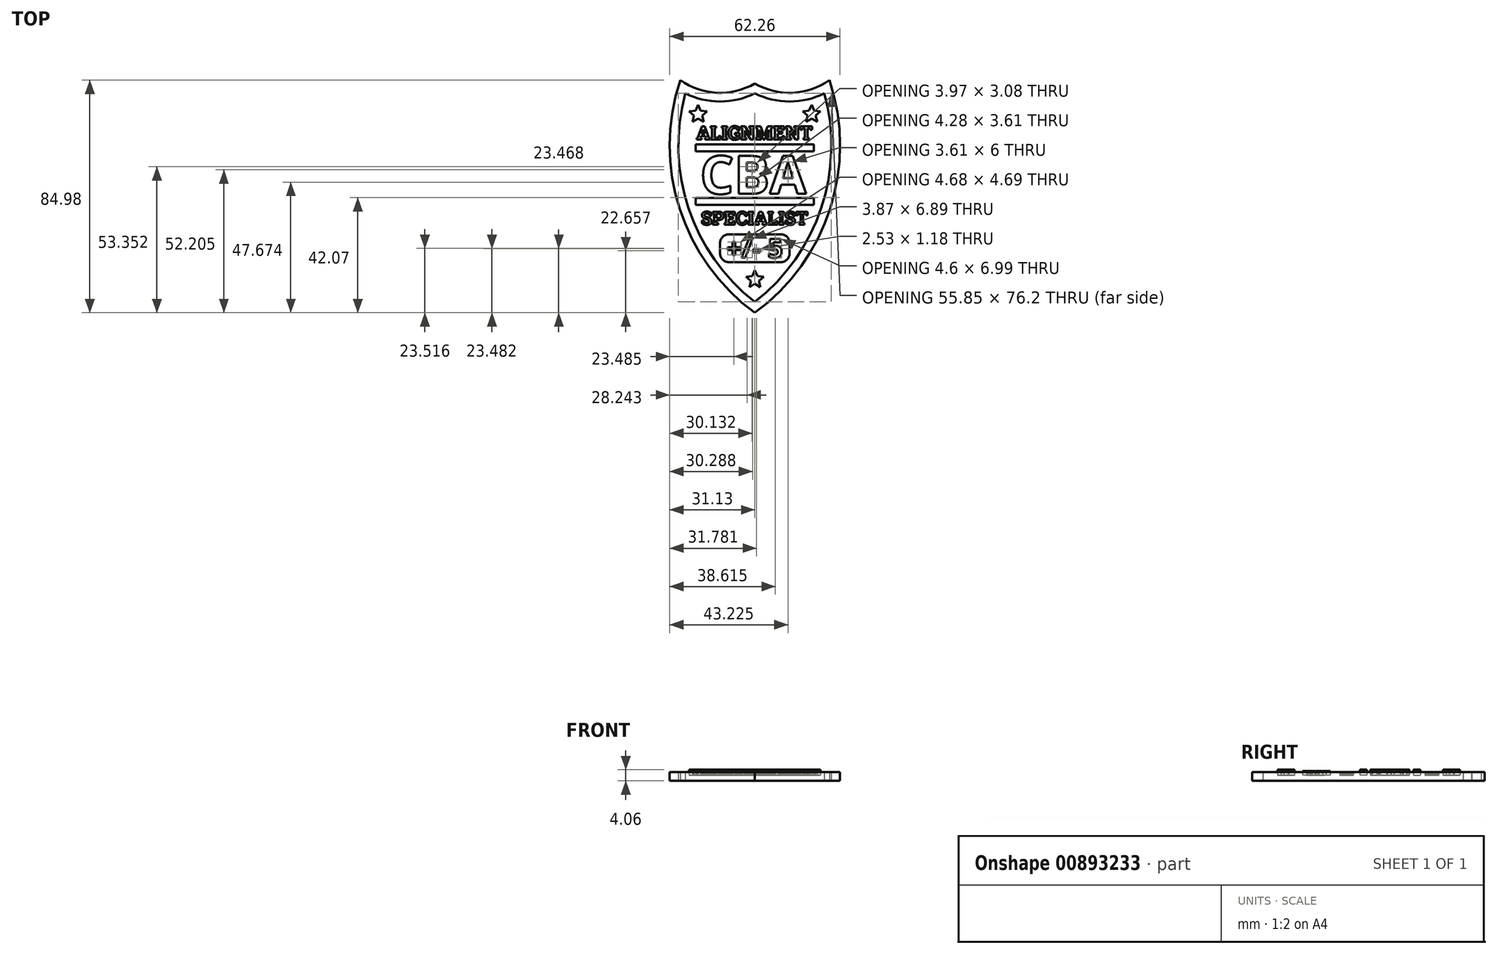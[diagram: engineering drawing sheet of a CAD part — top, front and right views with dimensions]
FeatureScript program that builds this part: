
annotation { "Feature Type Name" : "Feature", "Feature Type Description" : "" }
export const myFeature = defineFeature(function(context is Context, id is Id, definition is map)
    precondition{}
    {
        {
            var Q0;
            Q0=qCreatedBy(makeId("Top.planeOp"),FACE);
            cPlane(context, id + "F0", {"entities" : qUnion([Q0]), "cplaneType" : CPlaneType.OFFSET, "offset" : 2.03 * mm, "width" : 152.4 * mm, "height" : 152.4 * mm});
        }
        {
            var Q0;
            Q0=qCreatedBy(makeId("Top.planeOp"),FACE);
            var sketch = newSketch(context, id + "F1", { "sketchPlane" : qUnion([Q0])});
            skLineSegment(sketch, "E0.bottom", {"start": v(-25.4, 38.1) * mm, "end": v(25.4, 38.1) * mm, "construction": true});
            skLineSegment(sketch, "E0.top", {"start": v(-25.4, -38.1) * mm, "end": v(25.4, -38.1) * mm, "construction": true});
            skLineSegment(sketch, "E0.left", {"start": v(-25.4, 38.1) * mm, "end": v(-25.4, -38.1) * mm, "construction": true});
            skLineSegment(sketch, "E0.right", {"start": v(25.4, 38.1) * mm, "end": v(25.4, -38.1) * mm, "construction": true});
            skPoint(sketch, "E0.middle", {"position": v(0, 0) * mm});
            skLineSegment(sketch, "E1", {"start": v(0, 38.1) * mm, "end": v(0, 63.5) * mm, "construction": true});
            skPoint(sketch, "E1.endSnap0", {"position": v(0, 43.6) * mm});
            skLineSegment(sketch, "E2", {"start": v(0, 63.5) * mm, "end": v(12.7, 63.5) * mm, "construction": true});
            skLineSegment(sketch, "E3", {"start": v(12.7, 63.5) * mm, "end": v(0, 63.5) * mm, "construction": true});
            skArc(sketch, "E4", {"start": v(0, 38.1) * mm, "mid": v(12.7, 35.1) * mm, "end": v(25.4, 38.1) * mm});
            skArc(sketch, "E5", {"start": v(-25.4, 38.1) * mm, "mid": v(-15.62, 8.14) * mm, "end": v(9.94, -10.29) * mm, "construction": true});
            skArc(sketch, "E6", {"start": v(0, -38.1) * mm, "mid": v(24.24, -3.85) * mm, "end": v(25.4, 38.1) * mm});
            skLineSegment(sketch, "E7", {"start": v(0, 38.1) * mm, "end": v(0, -38.1) * mm});
            skArc(sketch, "E8.MirrorCS", {"start": v(0, -38.1) * mm, "mid": v(-24.24, -3.85) * mm, "end": v(-25.4, 38.1) * mm});
            skArc(sketch, "E9.MirrorCS", {"start": v(0, 38.1) * mm, "mid": v(-12.7, 35.1) * mm, "end": v(-25.4, 38.1) * mm});
            skSolve(sketch);
        }
        {
            var Q0;
            Q0=qCreatedBy(makeId("Top.planeOp"),FACE);
            var sketch = newSketch(context, id + "F2", { "sketchPlane" : qUnion([Q0])});
            skArc(sketch, "E10.0", {"start": v(0, 38.1) * mm, "mid": v(-12.7, 35.1) * mm, "end": v(-25.4, 38.1) * mm});
            skArc(sketch, "E11.0", {"start": v(0, 38.1) * mm, "mid": v(12.7, 35.1) * mm, "end": v(25.4, 38.1) * mm});
            skArc(sketch, "E12.0", {"start": v(0, -38.1) * mm, "mid": v(24.24, -3.85) * mm, "end": v(25.4, 38.1) * mm});
            skArc(sketch, "E13.0", {"start": v(0, -38.1) * mm, "mid": v(-24.24, -3.85) * mm, "end": v(-25.4, 38.1) * mm});
            skArc(sketch, "E14.0", {"start": v(0, 41.7) * mm, "mid": v(-13.8, 38.3) * mm, "end": v(-27.26, 42.9) * mm});
            skArc(sketch, "E14.1", {"start": v(0, 41.7) * mm, "mid": v(13.8, 38.3) * mm, "end": v(27.26, 42.9) * mm});
            skArc(sketch, "E14.2", {"start": v(0, -42.07) * mm, "mid": v(27.51, -4.04) * mm, "end": v(27.26, 42.9) * mm});
            skArc(sketch, "E14.3", {"start": v(0, -42.07) * mm, "mid": v(-27.51, -4.04) * mm, "end": v(-27.26, 42.9) * mm});
            skSolve(sketch);
        }
        {
            var Q0;
            Q0 = qSketchRegion(id + "F2", true);
            extrude(context, id + "F3", {"entities" : qUnion([Q0]), "depth" : 3.17 * mm, "offsetDistance" : 25.4 * mm});
        }
        {
            var Q0;
            Q0=qCreatedBy(id+"F0.planeOp",FACE);
            var sketch = newSketch(context, id + "F4", { "sketchPlane" : qUnion([Q0])});
            skLineSegment(sketch, "E15", {"start": v(-25.4, 15.35) * mm, "end": v(22.36, 15.35) * mm, "construction": true});
            skLineSegment(sketch, "E16", {"start": v(22.36, 15.35) * mm, "end": v(22.36, 1.37) * mm, "construction": true});
            skLineSegment(sketch, "E17", {"start": v(22.36, 1.37) * mm, "end": v(-25.4, 1.37) * mm, "construction": true});
            skLineSegment(sketch, "E18", {"start": v(-25.4, 1.37) * mm, "end": v(-25.4, 15.35) * mm, "construction": true});
            skText(sketch, "E19", { "text": "CBA", "fontName": "OpenSans-Bold.ttf"});
            skLineSegment(sketch, "E20", {"start": v(0, 0) * mm, "end": v(0, 38.1) * mm, "construction": true});
            skLineSegment(sketch, "E21.0", {"start": v(-21.59, 16.88) * mm, "end": v(21.6, 16.88) * mm});
            skLineSegment(sketch, "E22", {"start": v(-21.59, 16.88) * mm, "end": v(-21.59, 19.42) * mm});
            skLineSegment(sketch, "E23", {"start": v(-21.59, 19.42) * mm, "end": v(0, 19.42) * mm});
            skLineSegment(sketch, "E24", {"start": v(0, 19.42) * mm, "end": v(21.59, 19.42) * mm});
            skLineSegment(sketch, "E25", {"start": v(21.59, 19.42) * mm, "end": v(21.59, 16.88) * mm});
            skLineSegment(sketch, "E26", {"start": v(0, 15.35) * mm, "end": v(0, 1.37) * mm, "construction": true});
            skLineSegment(sketch, "E27", {"start": v(0, 8.36) * mm, "end": v(22.36, 8.36) * mm, "construction": true});
            skLineSegment(sketch, "E28.MirrorCS", {"start": v(-21.6, -2.69) * mm, "end": v(0, -2.69) * mm});
            skLineSegment(sketch, "E29.MirrorCS", {"start": v(0, -2.69) * mm, "end": v(21.59, -2.69) * mm});
            skLineSegment(sketch, "E30.MirrorCS", {"start": v(21.59, -2.69) * mm, "end": v(21.59, -0.15) * mm});
            skLineSegment(sketch, "E31.MirrorCS", {"start": v(-21.6, -0.15) * mm, "end": v(-21.6, -2.69) * mm});
            skLineSegment(sketch, "E32.MirrorCS", {"start": v(-21.59, -0.15) * mm, "end": v(21.59, -0.15) * mm});
            skCircle(sketch, "E33.cCircle", {"center": v(0, -29.93) * mm, "radius": 3.42 * mm, "construction": true});
            skLineSegment(sketch, "E33.0", {"start": v(0, -26.51) * mm, "end": v(3.25, -28.88) * mm, "construction": true});
            skLineSegment(sketch, "E33.1", {"start": v(3.25, -28.88) * mm, "end": v(2.01, -32.7) * mm, "construction": true});
            skLineSegment(sketch, "E33.2", {"start": v(2.01, -32.7) * mm, "end": v(-2.01, -32.7) * mm, "construction": true});
            skLineSegment(sketch, "E33.3", {"start": v(-2.01, -32.7) * mm, "end": v(-3.25, -28.88) * mm, "construction": true});
            skLineSegment(sketch, "E33.4", {"start": v(-3.25, -28.88) * mm, "end": v(0, -26.51) * mm, "construction": true});
            skCircle(sketch, "E34.cCircle", {"center": v(0, -29.93) * mm, "radius": 1.35 * mm, "construction": true});
            skLineSegment(sketch, "E34.0", {"start": v(0, -28.58) * mm, "end": v(1.28, -29.52) * mm, "construction": true});
            skLineSegment(sketch, "E34.1", {"start": v(1.28, -29.52) * mm, "end": v(0.8, -31.03) * mm, "construction": true});
            skLineSegment(sketch, "E34.2", {"start": v(0.8, -31.03) * mm, "end": v(-0.8, -31.03) * mm, "construction": true});
            skLineSegment(sketch, "E34.3", {"start": v(-0.8, -31.03) * mm, "end": v(-1.28, -29.52) * mm, "construction": true});
            skLineSegment(sketch, "E34.4", {"start": v(-1.28, -29.52) * mm, "end": v(0, -28.58) * mm, "construction": true});
            skLineSegment(sketch, "E35", {"start": v(-1.28, -29.52) * mm, "end": v(0, -26.51) * mm, "construction": true});
            skLineSegment(sketch, "E36", {"start": v(1.28, -29.52) * mm, "end": v(0, -26.51) * mm, "construction": true});
            skLineSegment(sketch, "E37", {"start": v(0, -28.58) * mm, "end": v(3.25, -28.88) * mm, "construction": true});
            skLineSegment(sketch, "E38", {"start": v(3.25, -28.88) * mm, "end": v(0.9, -30.95) * mm, "construction": true});
            skLineSegment(sketch, "E39", {"start": v(0.9, -30.95) * mm, "end": v(1.28, -29.52) * mm, "construction": true});
            skLineSegment(sketch, "E40", {"start": v(2.01, -32.7) * mm, "end": v(1.28, -29.52) * mm, "construction": true});
            skLineSegment(sketch, "E41", {"start": v(-0.8, -31.03) * mm, "end": v(2.01, -32.7) * mm, "construction": true});
            skLineSegment(sketch, "E42", {"start": v(-2.01, -32.7) * mm, "end": v(-1.28, -29.52) * mm, "construction": true});
            skLineSegment(sketch, "E43", {"start": v(-2.01, -32.7) * mm, "end": v(0.8, -31.03) * mm, "construction": true});
            skLineSegment(sketch, "E44", {"start": v(0, -28.58) * mm, "end": v(-3.25, -28.88) * mm, "construction": true});
            skLineSegment(sketch, "E45", {"start": v(-0.8, -31.03) * mm, "end": v(-3.25, -28.88) * mm, "construction": true});
            skLineSegment(sketch, "E46", {"start": v(-3.25, -28.88) * mm, "end": v(-0.92, -28.66) * mm});
            skLineSegment(sketch, "E47", {"start": v(-0.92, -28.66) * mm, "end": v(0, -26.51) * mm});
            skLineSegment(sketch, "E48", {"start": v(0, -26.51) * mm, "end": v(0.93, -28.67) * mm});
            skLineSegment(sketch, "E49", {"start": v(0.93, -28.67) * mm, "end": v(3.25, -28.88) * mm});
            skLineSegment(sketch, "E50", {"start": v(3.25, -28.88) * mm, "end": v(1.5, -30.42) * mm});
            skLineSegment(sketch, "E51", {"start": v(1.5, -30.42) * mm, "end": v(2.01, -32.7) * mm});
            skLineSegment(sketch, "E52", {"start": v(2.01, -32.7) * mm, "end": v(0, -31.5) * mm});
            skLineSegment(sketch, "E53", {"start": v(0, -31.5) * mm, "end": v(-2.01, -32.7) * mm});
            skLineSegment(sketch, "E54", {"start": v(-2.01, -32.7) * mm, "end": v(-1.5, -30.42) * mm});
            skLineSegment(sketch, "E55", {"start": v(-1.5, -30.42) * mm, "end": v(-3.25, -28.88) * mm});
            skArc(sketch, "E56.0", {"start": v(3.9, -33.09) * mm, "mid": v(-18.21, -1.84) * mm, "end": v(-19.27, 36.43) * mm, "construction": true});
            skLineSegment(sketch, "E57", {"start": v(0, 0) * mm, "end": v(-21.6, 0) * mm, "construction": true});
            skLineSegment(sketch, "E58", {"start": v(-21.6, 0) * mm, "end": v(-21.6, 5.6) * mm, "construction": true});
            skLineSegment(sketch, "E59", {"start": v(-21.6, 5.6) * mm, "end": v(-20.22, 5.6) * mm, "construction": true});
            skCircle(sketch, "E60.cCircle", {"center": v(-20.36, 5.58) * mm, "radius": 3.42 * mm, "construction": true});
            skLineSegment(sketch, "E60.0", {"start": v(-20.36, 9) * mm, "end": v(-17.11, 6.64) * mm, "construction": true});
            skLineSegment(sketch, "E60.1", {"start": v(-17.11, 6.64) * mm, "end": v(-18.35, 2.81) * mm, "construction": true});
            skLineSegment(sketch, "E60.2", {"start": v(-18.35, 2.81) * mm, "end": v(-22.37, 2.81) * mm, "construction": true});
            skLineSegment(sketch, "E60.3", {"start": v(-22.37, 2.81) * mm, "end": v(-23.62, 6.64) * mm, "construction": true});
            skLineSegment(sketch, "E60.4", {"start": v(-23.62, 6.64) * mm, "end": v(-20.36, 9) * mm, "construction": true});
            skCircle(sketch, "E61.cCircle", {"center": v(-20.36, 5.58) * mm, "radius": 1.35 * mm, "construction": true});
            skLineSegment(sketch, "E61.0", {"start": v(-20.36, 6.93) * mm, "end": v(-19.08, 6) * mm, "construction": true});
            skLineSegment(sketch, "E61.1", {"start": v(-19.08, 6) * mm, "end": v(-19.57, 4.49) * mm, "construction": true});
            skLineSegment(sketch, "E61.2", {"start": v(-19.57, 4.49) * mm, "end": v(-21.16, 4.49) * mm, "construction": true});
            skLineSegment(sketch, "E61.3", {"start": v(-21.16, 4.49) * mm, "end": v(-21.65, 6) * mm, "construction": true});
            skLineSegment(sketch, "E61.4", {"start": v(-21.65, 6) * mm, "end": v(-20.36, 6.93) * mm, "construction": true});
            skLineSegment(sketch, "E62", {"start": v(-21.65, 6) * mm, "end": v(-20.36, 9) * mm, "construction": true});
            skLineSegment(sketch, "E63", {"start": v(-19.08, 6) * mm, "end": v(-20.36, 9) * mm, "construction": true});
            skLineSegment(sketch, "E64", {"start": v(-20.36, 6.93) * mm, "end": v(-17.11, 6.64) * mm, "construction": true});
            skLineSegment(sketch, "E65", {"start": v(-17.11, 6.64) * mm, "end": v(-19.47, 4.57) * mm, "construction": true});
            skLineSegment(sketch, "E66", {"start": v(-19.47, 4.57) * mm, "end": v(-19.08, 6) * mm, "construction": true});
            skLineSegment(sketch, "E67", {"start": v(-18.35, 2.81) * mm, "end": v(-19.08, 6) * mm, "construction": true});
            skLineSegment(sketch, "E68", {"start": v(-21.16, 4.49) * mm, "end": v(-18.35, 2.81) * mm, "construction": true});
            skLineSegment(sketch, "E69", {"start": v(-22.37, 2.81) * mm, "end": v(-21.65, 6) * mm, "construction": true});
            skLineSegment(sketch, "E70", {"start": v(-22.37, 2.81) * mm, "end": v(-19.57, 4.49) * mm, "construction": true});
            skLineSegment(sketch, "E71", {"start": v(-20.36, 6.93) * mm, "end": v(-23.62, 6.64) * mm, "construction": true});
            skLineSegment(sketch, "E72", {"start": v(-21.16, 4.49) * mm, "end": v(-23.62, 6.64) * mm, "construction": true});
            skLineSegment(sketch, "E73", {"start": v(-23.62, 6.64) * mm, "end": v(-21.28, 6.85) * mm, "construction": true});
            skLineSegment(sketch, "E74", {"start": v(-21.28, 6.85) * mm, "end": v(-20.36, 9) * mm, "construction": true});
            skLineSegment(sketch, "E75", {"start": v(-20.36, 9) * mm, "end": v(-19.44, 6.85) * mm, "construction": true});
            skLineSegment(sketch, "E76", {"start": v(-19.44, 6.85) * mm, "end": v(-17.11, 6.64) * mm, "construction": true});
            skLineSegment(sketch, "E77", {"start": v(-17.11, 6.64) * mm, "end": v(-18.87, 5.1) * mm, "construction": true});
            skLineSegment(sketch, "E78", {"start": v(-18.87, 5.1) * mm, "end": v(-18.35, 2.81) * mm, "construction": true});
            skLineSegment(sketch, "E79", {"start": v(-18.35, 2.81) * mm, "end": v(-20.36, 4.02) * mm, "construction": true});
            skLineSegment(sketch, "E80", {"start": v(-20.36, 4.02) * mm, "end": v(-22.37, 2.81) * mm, "construction": true});
            skLineSegment(sketch, "E81", {"start": v(-22.37, 2.81) * mm, "end": v(-21.85, 5.1) * mm, "construction": true});
            skLineSegment(sketch, "E82", {"start": v(-21.85, 5.1) * mm, "end": v(-23.62, 6.64) * mm, "construction": true});
            skCircle(sketch, "E83.MirrorC", {"center": v(20.36, 5.58) * mm, "radius": 1.35 * mm, "construction": true});
            skLineSegment(sketch, "E84.MirrorCS", {"start": v(22.37, 2.81) * mm, "end": v(21.85, 5.1) * mm, "construction": true});
            skLineSegment(sketch, "E85.MirrorCS", {"start": v(21.85, 5.1) * mm, "end": v(23.62, 6.64) * mm, "construction": true});
            skLineSegment(sketch, "E86.MirrorCS", {"start": v(17.11, 6.64) * mm, "end": v(18.87, 5.1) * mm, "construction": true});
            skLineSegment(sketch, "E87.MirrorCS", {"start": v(19.44, 6.85) * mm, "end": v(17.11, 6.64) * mm, "construction": true});
            skLineSegment(sketch, "E88.MirrorCS", {"start": v(23.62, 6.64) * mm, "end": v(21.28, 6.85) * mm, "construction": true});
            skLineSegment(sketch, "E89.MirrorCS", {"start": v(20.36, 9) * mm, "end": v(19.44, 6.85) * mm, "construction": true});
            skLineSegment(sketch, "E90.MirrorCS", {"start": v(20.36, 4.02) * mm, "end": v(22.37, 2.81) * mm, "construction": true});
            skLineSegment(sketch, "E91.MirrorCS", {"start": v(18.87, 5.1) * mm, "end": v(18.35, 2.81) * mm, "construction": true});
            skLineSegment(sketch, "E92.MirrorCS", {"start": v(18.35, 2.81) * mm, "end": v(20.36, 4.02) * mm, "construction": true});
            skLineSegment(sketch, "E93.MirrorCS", {"start": v(21.28, 6.85) * mm, "end": v(20.36, 9) * mm, "construction": true});
            skLineSegment(sketch, "E94.MirrorCS", {"start": v(19.08, 6) * mm, "end": v(20.36, 9) * mm, "construction": true});
            skLineSegment(sketch, "E95.MirrorCS", {"start": v(17.11, 6.64) * mm, "end": v(19.47, 4.57) * mm, "construction": true});
            skLineSegment(sketch, "E96.MirrorCS", {"start": v(21.16, 4.49) * mm, "end": v(23.62, 6.64) * mm, "construction": true});
            skLineSegment(sketch, "E97.MirrorCS", {"start": v(20.36, 6.93) * mm, "end": v(19.08, 6) * mm, "construction": true});
            skLineSegment(sketch, "E98.MirrorCS", {"start": v(20.36, 6.93) * mm, "end": v(23.62, 6.64) * mm, "construction": true});
            skLineSegment(sketch, "E99.MirrorCS", {"start": v(18.35, 2.81) * mm, "end": v(22.37, 2.81) * mm, "construction": true});
            skCircle(sketch, "E100.MirrorC", {"center": v(20.36, 5.58) * mm, "radius": 3.42 * mm, "construction": true});
            skLineSegment(sketch, "E101.MirrorCS", {"start": v(22.37, 2.81) * mm, "end": v(19.57, 4.49) * mm, "construction": true});
            skLineSegment(sketch, "E102.MirrorCS", {"start": v(21.16, 4.49) * mm, "end": v(18.35, 2.81) * mm, "construction": true});
            skLineSegment(sketch, "E103.MirrorCS", {"start": v(21.65, 6) * mm, "end": v(20.36, 9) * mm, "construction": true});
            skLineSegment(sketch, "E104.MirrorCS", {"start": v(20.36, 9) * mm, "end": v(17.11, 6.64) * mm, "construction": true});
            skLineSegment(sketch, "E105.MirrorCS", {"start": v(20.36, 6.93) * mm, "end": v(17.11, 6.64) * mm, "construction": true});
            skLineSegment(sketch, "E106.MirrorCS", {"start": v(22.37, 2.81) * mm, "end": v(23.62, 6.64) * mm, "construction": true});
            skLineSegment(sketch, "E107.MirrorCS", {"start": v(23.62, 6.64) * mm, "end": v(20.36, 9) * mm, "construction": true});
            skLineSegment(sketch, "E108.MirrorCS", {"start": v(21.6, 5.6) * mm, "end": v(20.22, 5.6) * mm, "construction": true});
            skLineSegment(sketch, "E109.MirrorCS", {"start": v(19.57, 4.49) * mm, "end": v(21.16, 4.49) * mm, "construction": true});
            skLineSegment(sketch, "E110.MirrorCS", {"start": v(21.16, 4.49) * mm, "end": v(21.65, 6) * mm, "construction": true});
            skLineSegment(sketch, "E111.MirrorCS", {"start": v(19.08, 6) * mm, "end": v(19.57, 4.49) * mm, "construction": true});
            skLineSegment(sketch, "E112.MirrorCS", {"start": v(18.35, 2.81) * mm, "end": v(19.08, 6) * mm, "construction": true});
            skLineSegment(sketch, "E113.MirrorCS", {"start": v(19.47, 4.57) * mm, "end": v(19.08, 6) * mm, "construction": true});
            skLineSegment(sketch, "E114.MirrorCS", {"start": v(17.11, 6.64) * mm, "end": v(18.35, 2.81) * mm, "construction": true});
            skLineSegment(sketch, "E115.MirrorCS", {"start": v(22.37, 2.81) * mm, "end": v(21.65, 6) * mm, "construction": true});
            skLineSegment(sketch, "E116.MirrorCS", {"start": v(21.65, 6) * mm, "end": v(20.36, 6.93) * mm, "construction": true});
            skLineSegment(sketch, "E117", {"start": v(-20.6, 30.48) * mm, "end": v(0, 30.48) * mm, "construction": true});
            skLineSegment(sketch, "E118", {"start": v(-21.98, 30.48) * mm, "end": v(-20.6, 30.48) * mm, "construction": true});
            skCircle(sketch, "E119.cCircle", {"center": v(-20.75, 30.46) * mm, "radius": 3.42 * mm, "construction": true});
            skLineSegment(sketch, "E119.0", {"start": v(-20.75, 33.89) * mm, "end": v(-17.5, 31.52) * mm, "construction": true});
            skLineSegment(sketch, "E119.1", {"start": v(-17.5, 31.52) * mm, "end": v(-18.74, 27.7) * mm, "construction": true});
            skLineSegment(sketch, "E119.2", {"start": v(-18.74, 27.7) * mm, "end": v(-22.76, 27.7) * mm, "construction": true});
            skLineSegment(sketch, "E119.3", {"start": v(-22.76, 27.7) * mm, "end": v(-24, 31.52) * mm, "construction": true});
            skLineSegment(sketch, "E119.4", {"start": v(-24, 31.52) * mm, "end": v(-20.75, 33.89) * mm, "construction": true});
            skCircle(sketch, "E120.cCircle", {"center": v(-20.75, 30.46) * mm, "radius": 1.35 * mm, "construction": true});
            skLineSegment(sketch, "E120.0", {"start": v(-20.75, 31.82) * mm, "end": v(-19.47, 30.88) * mm, "construction": true});
            skLineSegment(sketch, "E120.1", {"start": v(-19.47, 30.88) * mm, "end": v(-19.96, 29.37) * mm, "construction": true});
            skLineSegment(sketch, "E120.2", {"start": v(-19.96, 29.37) * mm, "end": v(-21.55, 29.37) * mm, "construction": true});
            skLineSegment(sketch, "E120.3", {"start": v(-21.55, 29.37) * mm, "end": v(-22.04, 30.88) * mm, "construction": true});
            skLineSegment(sketch, "E120.4", {"start": v(-22.04, 30.88) * mm, "end": v(-20.75, 31.82) * mm, "construction": true});
            skLineSegment(sketch, "E121", {"start": v(-22.04, 30.88) * mm, "end": v(-20.75, 33.89) * mm, "construction": true});
            skLineSegment(sketch, "E122", {"start": v(-19.47, 30.88) * mm, "end": v(-20.75, 33.89) * mm, "construction": true});
            skLineSegment(sketch, "E123", {"start": v(-20.75, 31.82) * mm, "end": v(-17.5, 31.52) * mm, "construction": true});
            skLineSegment(sketch, "E124", {"start": v(-17.5, 31.52) * mm, "end": v(-19.86, 29.45) * mm, "construction": true});
            skLineSegment(sketch, "E125", {"start": v(-19.86, 29.45) * mm, "end": v(-19.47, 30.88) * mm, "construction": true});
            skLineSegment(sketch, "E126", {"start": v(-18.74, 27.7) * mm, "end": v(-19.47, 30.88) * mm, "construction": true});
            skLineSegment(sketch, "E127", {"start": v(-21.55, 29.37) * mm, "end": v(-18.74, 27.7) * mm, "construction": true});
            skLineSegment(sketch, "E128", {"start": v(-22.76, 27.7) * mm, "end": v(-22.04, 30.88) * mm, "construction": true});
            skLineSegment(sketch, "E129", {"start": v(-22.76, 27.7) * mm, "end": v(-19.96, 29.37) * mm, "construction": true});
            skLineSegment(sketch, "E130", {"start": v(-20.75, 31.82) * mm, "end": v(-24, 31.52) * mm, "construction": true});
            skLineSegment(sketch, "E131", {"start": v(-21.55, 29.37) * mm, "end": v(-24, 31.52) * mm, "construction": true});
            skLineSegment(sketch, "E132", {"start": v(-24, 31.52) * mm, "end": v(-21.67, 31.73) * mm});
            skLineSegment(sketch, "E133", {"start": v(-21.67, 31.73) * mm, "end": v(-20.75, 33.89) * mm});
            skLineSegment(sketch, "E134", {"start": v(-20.75, 33.89) * mm, "end": v(-19.83, 31.73) * mm});
            skLineSegment(sketch, "E135", {"start": v(-19.83, 31.73) * mm, "end": v(-17.5, 31.52) * mm});
            skLineSegment(sketch, "E136", {"start": v(-17.5, 31.52) * mm, "end": v(-19.26, 29.98) * mm});
            skLineSegment(sketch, "E137", {"start": v(-19.26, 29.98) * mm, "end": v(-18.74, 27.7) * mm});
            skLineSegment(sketch, "E138", {"start": v(-18.74, 27.7) * mm, "end": v(-20.75, 28.9) * mm});
            skLineSegment(sketch, "E139", {"start": v(-20.75, 28.9) * mm, "end": v(-22.76, 27.7) * mm});
            skLineSegment(sketch, "E140", {"start": v(-22.76, 27.7) * mm, "end": v(-22.24, 29.98) * mm});
            skLineSegment(sketch, "E141", {"start": v(-22.24, 29.98) * mm, "end": v(-24, 31.52) * mm});
            skLineSegment(sketch, "E142.MirrorCS", {"start": v(17.5, 31.52) * mm, "end": v(19.26, 29.98) * mm});
            skLineSegment(sketch, "E143.MirrorCS", {"start": v(19.86, 29.45) * mm, "end": v(19.47, 30.88) * mm, "construction": true});
            skLineSegment(sketch, "E144.MirrorCS", {"start": v(20.75, 31.82) * mm, "end": v(19.47, 30.88) * mm, "construction": true});
            skLineSegment(sketch, "E145.MirrorCS", {"start": v(21.98, 30.48) * mm, "end": v(20.6, 30.48) * mm, "construction": true});
            skLineSegment(sketch, "E146.MirrorCS", {"start": v(22.04, 30.88) * mm, "end": v(20.75, 31.82) * mm, "construction": true});
            skLineSegment(sketch, "E147.MirrorCS", {"start": v(19.47, 30.88) * mm, "end": v(19.96, 29.37) * mm, "construction": true});
            skLineSegment(sketch, "E148.MirrorCS", {"start": v(21.55, 29.37) * mm, "end": v(22.04, 30.88) * mm, "construction": true});
            skLineSegment(sketch, "E149.MirrorCS", {"start": v(19.96, 29.37) * mm, "end": v(21.55, 29.37) * mm, "construction": true});
            skCircle(sketch, "E150.MirrorC", {"center": v(20.75, 30.46) * mm, "radius": 1.35 * mm, "construction": true});
            skLineSegment(sketch, "E151.MirrorCS", {"start": v(17.5, 31.52) * mm, "end": v(19.86, 29.45) * mm, "construction": true});
            skLineSegment(sketch, "E152.MirrorCS", {"start": v(19.26, 29.98) * mm, "end": v(18.74, 27.7) * mm});
            skLineSegment(sketch, "E153.MirrorCS", {"start": v(22.24, 29.98) * mm, "end": v(24, 31.52) * mm});
            skLineSegment(sketch, "E154.MirrorCS", {"start": v(18.74, 27.7) * mm, "end": v(20.75, 28.9) * mm});
            skLineSegment(sketch, "E155.MirrorCS", {"start": v(21.55, 29.37) * mm, "end": v(18.74, 27.7) * mm, "construction": true});
            skLineSegment(sketch, "E156.MirrorCS", {"start": v(21.55, 29.37) * mm, "end": v(24, 31.52) * mm, "construction": true});
            skLineSegment(sketch, "E157.MirrorCS", {"start": v(18.74, 27.7) * mm, "end": v(19.47, 30.88) * mm, "construction": true});
            skLineSegment(sketch, "E158.MirrorCS", {"start": v(24, 31.52) * mm, "end": v(21.67, 31.73) * mm});
            skLineSegment(sketch, "E159.MirrorCS", {"start": v(20.75, 33.89) * mm, "end": v(19.83, 31.73) * mm});
            skLineSegment(sketch, "E160.MirrorCS", {"start": v(22.76, 27.7) * mm, "end": v(22.24, 29.98) * mm});
            skLineSegment(sketch, "E161.MirrorCS", {"start": v(21.67, 31.73) * mm, "end": v(20.75, 33.89) * mm});
            skLineSegment(sketch, "E162.MirrorCS", {"start": v(20.75, 28.9) * mm, "end": v(22.76, 27.7) * mm});
            skLineSegment(sketch, "E163.MirrorCS", {"start": v(19.83, 31.73) * mm, "end": v(17.5, 31.52) * mm});
            skLineSegment(sketch, "E164.MirrorCS", {"start": v(22.04, 30.88) * mm, "end": v(20.75, 33.89) * mm, "construction": true});
            skLineSegment(sketch, "E165.MirrorCS", {"start": v(22.76, 27.7) * mm, "end": v(19.96, 29.37) * mm, "construction": true});
            skLineSegment(sketch, "E166.MirrorCS", {"start": v(18.74, 27.7) * mm, "end": v(22.76, 27.7) * mm, "construction": true});
            skLineSegment(sketch, "E167.MirrorCS", {"start": v(20.75, 31.82) * mm, "end": v(17.5, 31.52) * mm, "construction": true});
            skLineSegment(sketch, "E168.MirrorCS", {"start": v(20.75, 31.82) * mm, "end": v(24, 31.52) * mm, "construction": true});
            skLineSegment(sketch, "E169.MirrorCS", {"start": v(22.76, 27.7) * mm, "end": v(24, 31.52) * mm, "construction": true});
            skLineSegment(sketch, "E170.MirrorCS", {"start": v(22.76, 27.7) * mm, "end": v(22.04, 30.88) * mm, "construction": true});
            skLineSegment(sketch, "E171.MirrorCS", {"start": v(17.5, 31.52) * mm, "end": v(18.74, 27.7) * mm, "construction": true});
            skLineSegment(sketch, "E172.MirrorCS", {"start": v(19.47, 30.88) * mm, "end": v(20.75, 33.89) * mm, "construction": true});
            skLineSegment(sketch, "E173.MirrorCS", {"start": v(20.75, 33.89) * mm, "end": v(17.5, 31.52) * mm, "construction": true});
            skLineSegment(sketch, "E174.MirrorCS", {"start": v(24, 31.52) * mm, "end": v(20.75, 33.89) * mm, "construction": true});
            skCircle(sketch, "E175.MirrorC", {"center": v(20.75, 30.46) * mm, "radius": 3.42 * mm, "construction": true});
            const initialGuessF4  = {"E19": [-0.02004, 0.00137, 1, 0, 0.01398]};
            skSetInitialGuess(sketch, initialGuessF4);
            skSolve(sketch);
        }
        {
            var Q0;
            Q0 = qSketchRegion(id + "F4", true);
            extrude(context, id + "F5", {"entities" : qUnion([Q0]), "depth" : 2.03 * mm, "offsetDistance" : 25.4 * mm});
        }
        {
            var Q0;
            Q0=qCreatedBy(id+"F0.planeOp",FACE);
            var Q1;
            Q1=qCreatedBy(id+"F0.planeOp",FACE);
            var sketch = newSketch(context, id + "F6", { "sketchPlane" : qUnion([Q0, Q1])});
            skPoint(sketch, "E176.0", {"position": v(0, 0) * mm});
            skArc(sketch, "E177.0", {"start": v(0, -38.1) * mm, "mid": v(-24.24, -3.85) * mm, "end": v(-25.4, 38.1) * mm, "construction": true});
            skArc(sketch, "E178.0", {"start": v(0, -38.1) * mm, "mid": v(24.24, -3.85) * mm, "end": v(25.4, 38.1) * mm, "construction": true});
            skLineSegment(sketch, "E179", {"start": v(-25.4, 0) * mm, "end": v(25.4, 0) * mm, "construction": true});
            skLineSegment(sketch, "E180.bottom", {"start": v(9.53, -13.4) * mm, "end": v(-9.53, -13.4) * mm});
            skLineSegment(sketch, "E180.top", {"start": v(9.53, -23.56) * mm, "end": v(-9.53, -23.56) * mm});
            skLineSegment(sketch, "E180.left", {"start": v(12.7, -16.57) * mm, "end": v(12.7, -20.38) * mm});
            skLineSegment(sketch, "E180.right", {"start": v(-12.7, -16.57) * mm, "end": v(-12.7, -20.38) * mm});
            skPoint(sketch, "E180.middle", {"position": v(0, -18.48) * mm});
            skPoint(sketch, "E181.visualSharp", {"position": v(-12.7, -13.4) * mm});
            skArc(sketch, "E181.filletArc", {"start": v(-9.53, -13.4) * mm, "mid": v(-11.77, -14.33) * mm, "end": v(-12.7, -16.57) * mm});
            skPoint(sketch, "E182.visualSharp", {"position": v(-12.7, -23.56) * mm});
            skArc(sketch, "E182.filletArc", {"start": v(-12.7, -20.38) * mm, "mid": v(-11.77, -22.63) * mm, "end": v(-9.53, -23.56) * mm});
            skPoint(sketch, "E183.visualSharp", {"position": v(12.7, -13.4) * mm});
            skArc(sketch, "E183.filletArc", {"start": v(12.7, -16.57) * mm, "mid": v(11.77, -14.33) * mm, "end": v(9.53, -13.4) * mm});
            skPoint(sketch, "E184.visualSharp", {"position": v(12.7, -23.56) * mm});
            skArc(sketch, "E184.filletArc", {"start": v(9.53, -23.56) * mm, "mid": v(11.77, -22.63) * mm, "end": v(12.7, -20.38) * mm});
            skArc(sketch, "E185.0", {"start": v(20.74, 29.7) * mm, "mid": v(10.26, 28.84) * mm, "end": v(0, 31.16) * mm, "construction": true});
            skArc(sketch, "E185.1", {"start": v(0, -29.8) * mm, "mid": v(17.92, -2.69) * mm, "end": v(20.74, 29.7) * mm, "construction": true});
            skArc(sketch, "E185.2", {"start": v(-20.74, 29.7) * mm, "mid": v(-17.92, -2.69) * mm, "end": v(0, -29.8) * mm, "construction": true});
            skArc(sketch, "E185.3", {"start": v(0, 31.16) * mm, "mid": v(-10.26, 28.84) * mm, "end": v(-20.74, 29.7) * mm, "construction": true});
            skLineSegment(sketch, "E186", {"start": v(0, -15.06) * mm, "end": v(0, -13.4) * mm, "construction": true});
            skText(sketch, "E187", { "text": "+/- 5", "fontName": "OpenSans-Bold.ttf"});
            const initialGuessF6  = {"E187": [-0.0104, -0.022, 1, 0, 0.00695]};
            skSetInitialGuess(sketch, initialGuessF6);
            skSolve(sketch);
        }
        {
            var Q0;
            Q0 = qSketchRegion(id + "F6", true);
            extrude(context, id + "F7", {"entities" : qUnion([Q0]), "depth" : 1.52 * mm, "offsetDistance" : 25.4 * mm});
        }
        {
            var Q0;
            Q0=qCreatedBy(id+"F0.planeOp",FACE);
            var Q1;
            Q1=qCreatedBy(id+"F0.planeOp",FACE);
            var sketch = newSketch(context, id + "F8", { "sketchPlane" : qUnion([Q0, Q1])});
            skLineSegment(sketch, "E188", {"start": v(0, -3.27) * mm, "end": v(-9.48, -3.27) * mm, "construction": true});
            skLineSegment(sketch, "E189", {"start": v(0, 0) * mm, "end": v(0, -3.27) * mm, "construction": true});
            skLineSegment(sketch, "E190.MirrorCS", {"start": v(0, -3.27) * mm, "end": v(9.48, -3.27) * mm, "construction": true});
            skText(sketch, "E191", { "text": "ALIGNMENT", "fontName": "RobotoSlab-Bold.ttf"});
            skText(sketch, "E192", { "text": "SPECIALIST", "fontName": "RobotoSlab-Bold.ttf"});
            const initialGuessF8  = {"E191": [-0.02134, 0.02117, 1, 0, 0.005], "E192": [-0.01968, -0.00992, 1, 0, 0.00484]};
            skSetInitialGuess(sketch, initialGuessF8);
            skSolve(sketch);
        }
        {
            var Q0;
            Q0 = qSketchRegion(id + "F8", true);
            extrude(context, id + "F9", {"entities" : qUnion([Q0]), "depth" : 1.02 * mm, "offsetDistance" : 25.4 * mm});
        }
    });
